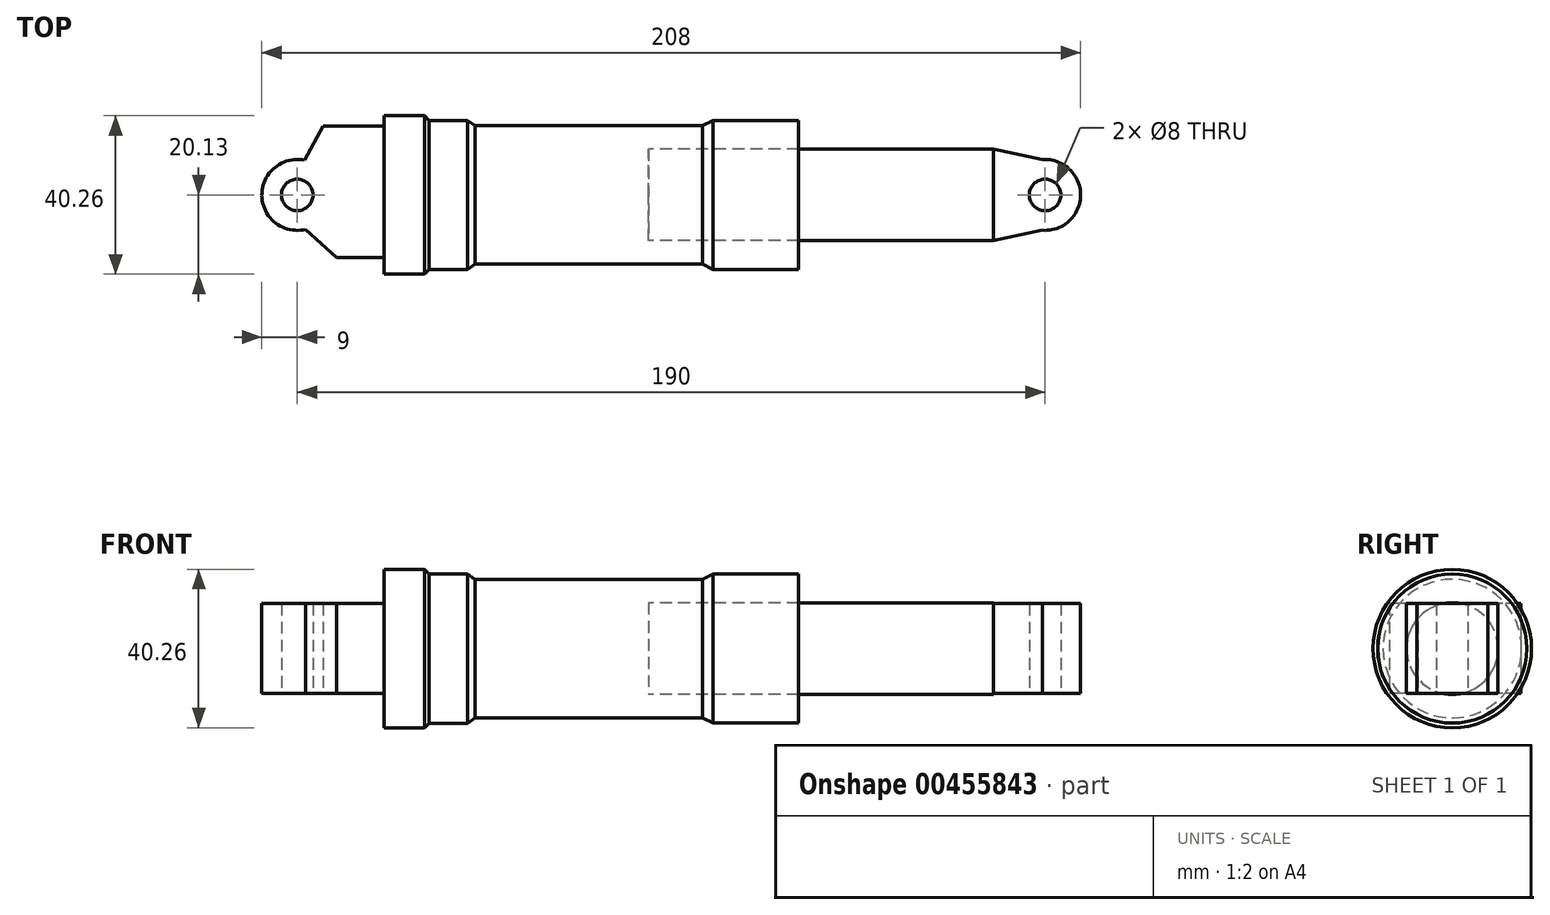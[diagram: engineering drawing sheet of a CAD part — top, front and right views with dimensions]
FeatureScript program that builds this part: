
annotation { "Feature Type Name" : "Feature", "Feature Type Description" : "" }
export const myFeature = defineFeature(function(context is Context, id is Id, definition is map)
    precondition{}
    {
        {
            var Q0;
            Q0=qCreatedBy(makeId("Top.planeOp"),FACE);
            var sketch = newSketch(context, id + "F0", { "sketchPlane" : qUnion([Q0])});
            skLineSegment(sketch, "E0", {"start": v(8, 17.6) * mm, "end": v(-49.88, 17.6) * mm});
            skLineSegment(sketch, "E1", {"start": v(-49.88, 17.6) * mm, "end": v(-51.74, 18.95) * mm});
            skLineSegment(sketch, "E2", {"start": v(-51.74, 18.95) * mm, "end": v(-61.56, 18.95) * mm});
            skLineSegment(sketch, "E3", {"start": v(-61.56, 18.95) * mm, "end": v(-62.64, 20.13) * mm});
            skLineSegment(sketch, "E4", {"start": v(-62.64, 20.13) * mm, "end": v(-72.9, 20.13) * mm});
            skLineSegment(sketch, "E5", {"start": v(-72.9, 20.13) * mm, "end": v(-72.9, 0) * mm});
            skLineSegment(sketch, "E6", {"start": v(-72.9, 17.45) * mm, "end": v(-88.37, 17.45) * mm});
            skLineSegment(sketch, "E7", {"start": v(-88.37, 17.45) * mm, "end": v(-93.1, 8.8) * mm});
            skLineSegment(sketch, "E8", {"start": v(8, 17.6) * mm, "end": v(10.59, 18.94) * mm});
            skLineSegment(sketch, "E9", {"start": v(10.59, 18.94) * mm, "end": v(32.37, 18.94) * mm});
            skLineSegment(sketch, "E10", {"start": v(32.37, 18.94) * mm, "end": v(32.37, 0) * mm});
            skCircle(sketch, "E11", {"center": v(95, 0) * mm, "radius": 4 * mm});
            skCircle(sketch, "E12", {"center": v(-95, 0) * mm, "radius": 4 * mm});
            skArc(sketch, "E13", {"start": v(-93.1, 8.8) * mm, "mid": v(-104, -0.13) * mm, "end": v(-92.85, -8.74) * mm});
            skArc(sketch, "E14", {"start": v(94.3, -8.97) * mm, "mid": v(104, 0) * mm, "end": v(94.3, 8.97) * mm});
            skLineSegment(sketch, "E15", {"start": v(94.3, 8.97) * mm, "end": v(81.82, 11.63) * mm});
            skLineSegment(sketch, "E16", {"start": v(81.82, 11.63) * mm, "end": v(-5.73, 11.63) * mm});
            skLineSegment(sketch, "E17", {"start": v(-5.73, 11.63) * mm, "end": v(-5.73, 0) * mm});
            skLineSegment(sketch, "E18", {"start": v(81.82, 11.63) * mm, "end": v(81.82, 0) * mm});
            skLineSegment(sketch, "E19.MirrorCS", {"start": v(81.82, -11.63) * mm, "end": v(81.82, 0) * mm});
            skLineSegment(sketch, "E20.MirrorCS", {"start": v(94.3, -8.97) * mm, "end": v(81.82, -11.63) * mm});
            skLineSegment(sketch, "E21", {"start": v(-92.85, -8.74) * mm, "end": v(-84.95, -15.95) * mm});
            skLineSegment(sketch, "E22", {"start": v(-84.95, -15.95) * mm, "end": v(-72.9, -15.95) * mm});
            skLineSegment(sketch, "E23.MirrorCS", {"start": v(-72.9, -15.95) * mm, "end": v(-72.9, 0) * mm});
            skPoint(sketch, "E24.orphan", {"position": v(-72.9, -20.13) * mm});
            skLineSegment(sketch, "E25.trimOffspring", {"start": v(-72.9, 0) * mm, "end": v(81.82, 0) * mm});
            skSolve(sketch);
        }
        {
            var Q0;
            Q0=makeQuery(id+"F0.imprint","IMPRINT",FACE,{"disambiguationData":[TD([[makeQuery(id+"F0.imprint","IMPRINT",EDGE,{"derivedFrom":sQuery(id+"F0.wireOp",EDGE,"E0")}),1.0]])]});
            var Q1;
            {var subQ5=sQuery(id+"F0.wireOp",EDGE,"E17");Q1=makeQuery(id+"F0.imprint","IMPRINT",FACE,{"disambiguationData":[TD([[makeQuery(id+"F0.imprint","IMPRINT",EDGE,{"derivedFrom":subQ5}),1.0]])]});}
            var Q2;
            Q2=sQuery(id+"F0.wireOp",EDGE,"E25.trimOffspring");
            revolve(context, id + "F1", {"entities" : qUnion([Q0, Q1]), "axis" : qUnion([Q2]), "revolveType" : RevolveType.FULL});
        }
        {
            var Q0;
            {var subQ5=sQuery(id+"F0.wireOp",EDGE,"E18");Q0=makeQuery(id+"F0.imprint","IMPRINT",FACE,{"disambiguationData":[TD([[makeQuery(id+"F0.imprint","IMPRINT",EDGE,{"derivedFrom":subQ5}),-1.0]])]});}
            var Q1;
            {var subQ5=sQuery(id+"F0.wireOp",EDGE,"E17");Q1=makeQuery(id+"F0.imprint","IMPRINT",FACE,{"disambiguationData":[TD([[makeQuery(id+"F0.imprint","IMPRINT",EDGE,{"derivedFrom":subQ5}),1.0]])]});}
            var Q2;
            Q2=sQuery(id+"F0.wireOp",EDGE,"E25.trimOffspring");
            revolve(context, id + "F2", {"entities" : qUnion([Q0, Q1]), "axis" : qUnion([Q2]), "revolveType" : RevolveType.FULL});
        }
        {
            var Q0;
            Q0=makeQuery(id+"F0.imprint","IMPRINT",FACE,{"disambiguationData":[TD([[makeQuery(id+"F0.imprint","IMPRINT",EDGE,{"derivedFrom":sQuery(id+"F0.wireOp",EDGE,"E11")}),-1.0]])]});
            extrude(context, id + "F3", {"entities" : qUnion([Q0]), "operationType" : NewBodyOperationType.ADD, "depth" : 11.43 * mm, "offsetDistance" : 25.4 * mm, "hasSecondDirection" : true, "secondDirectionOppositeDirection" : true, "secondDirectionDepth" : 11.43 * mm});
        }
        {
            var Q0;
            {var subQ0=sQuery(id+"F0.wireOp",EDGE,"E6");Q0=makeQuery(id+"F0.imprint","IMPRINT",FACE,{"disambiguationData":[TD([[makeQuery(id+"F0.imprint","IMPRINT",EDGE,{"derivedFrom":subQ0}),1.0]])]});}
            extrude(context, id + "F4", {"entities" : qUnion([Q0]), "operationType" : NewBodyOperationType.ADD, "depth" : 11.43 * mm, "offsetDistance" : 25.4 * mm, "hasSecondDirection" : true, "secondDirectionOppositeDirection" : true, "secondDirectionDepth" : 11.43 * mm});
        }
    });
